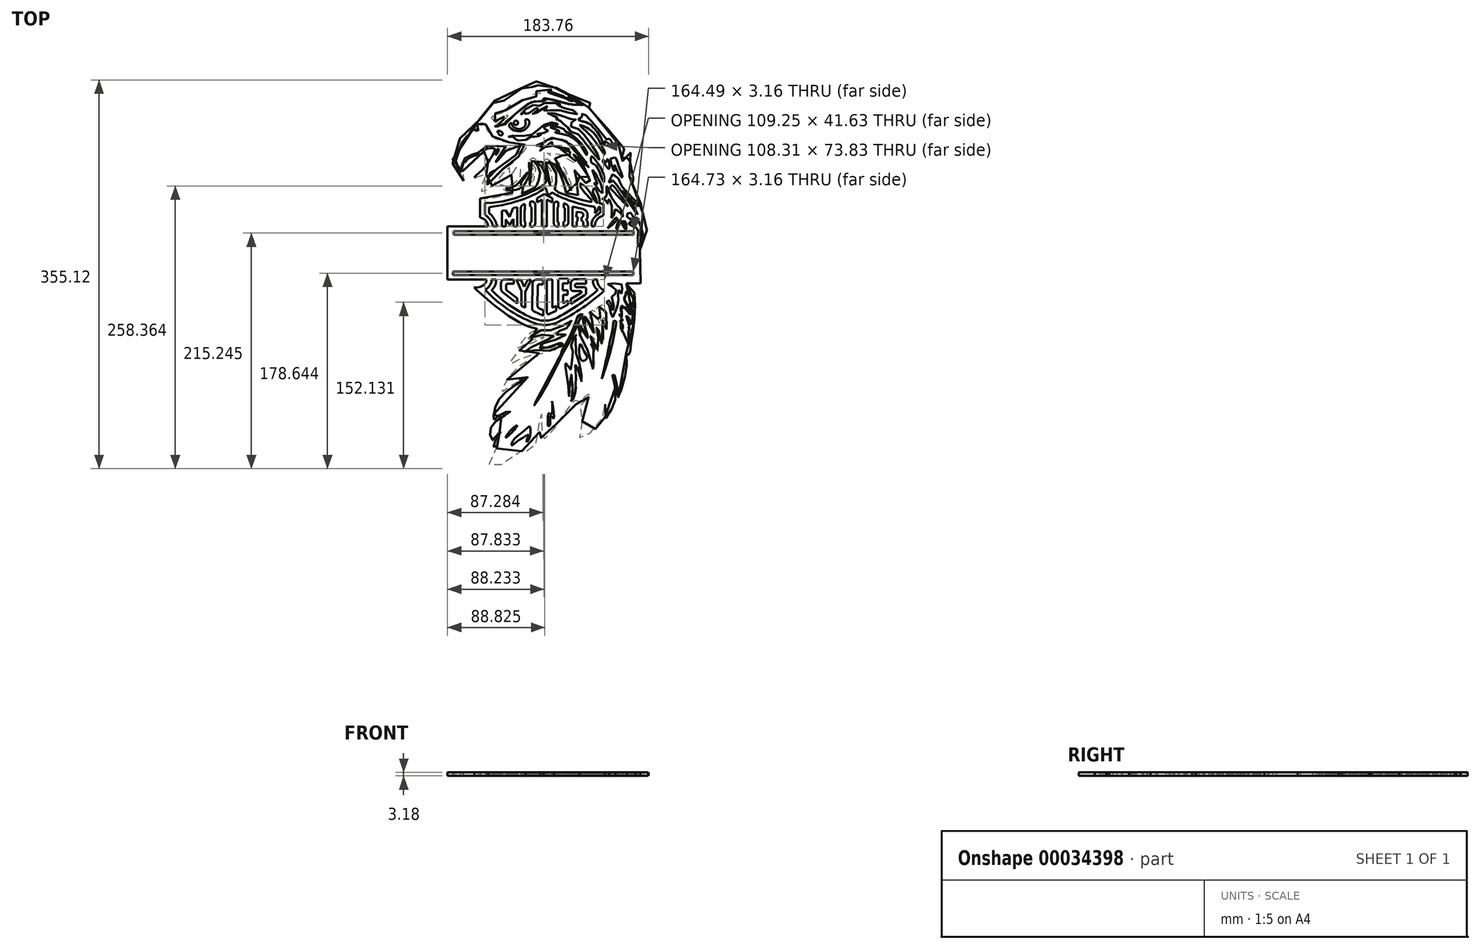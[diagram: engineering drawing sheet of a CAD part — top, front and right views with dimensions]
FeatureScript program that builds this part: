
annotation { "Feature Type Name" : "Feature", "Feature Type Description" : "" }
export const myFeature = defineFeature(function(context is Context, id is Id, definition is map)
    precondition{}
    {
        {
            var Q0;
            Q0=qCreatedBy(makeId("Top.planeOp"),FACE);
            var sketch = newSketch(context, id + "F0", { "sketchPlane" : qUnion([Q0])});
            skFitSpline(sketch, "E0", {"points": [v(60.89, -122.96) * mm, v(51.54, -129.24) * mm, v(44.36, -139.49) * mm, v(55.14, -133.02) * mm, v(69.7, -129.07) * mm, v(55.86, -135.35) * mm, v(43.46, -143.98) * mm, v(37, -153.68) * mm, v(50.3, -147.75) * mm, v(67.55, -144.16) * mm, v(55.18, -149.98) * mm, v(34.66, -167.88) * mm, v(29.99, -179.02) * mm, v(39.87, -172.37) * mm, v(53.35, -166.08) * mm, v(35.2, -177.94) * mm, v(23.52, -194.12) * mm, v(22.27, -204.72) * mm, v(27.48, -200.59) * mm, v(37.36, -197.35) * mm, v(26.76, -204.36) * mm, v(18.86, -216.58) * mm, v(21.56, -223.77) * mm, v(22.81, -221.8) * mm, v(29.28, -215.14) * mm, v(23.17, -225.03) * mm, v(22.82, -230.6) * mm, v(24.97, -227.72) * mm, v(24.61, -232.75) * mm, v(17.71, -249.36) * mm, v(47.08, -234.2) * mm, v(50.68, -230.06) * mm, v(51.76, -230.42) * mm, v(51.76, -234.91) * mm, v(61.28, -226.47) * mm, v(64.5, -198.97) * mm, v(64.69, -197.35) * mm, v(67.75, -211.73) * mm, v(65.06, -224.85) * mm, v(72.96, -218.56) * mm, v(77.45, -213.7) * mm, v(76.91, -210.3) * mm, v(79.97, -208.67) * mm, v(89.85, -194.66) * mm, v(95.42, -189.63) * mm, v(96.86, -187.1) * mm, v(97.76, -191.6) * mm, v(101.71, -185.85) * mm, v(106.38, -183.16) * mm, v(112.5, -178.48) * mm, v(106.56, -186.75) * mm, v(101.9, -190.34) * mm, v(101.72, -204.36) * mm, v(103.51, -202.2) * mm, v(102.98, -208.31) * mm, v(101.6, -214.92) * mm, v(100.96, -222.3) * mm, v(108.91, -218.2) * mm, v(121.85, -203.46) * mm, v(123.64, -190.7) * mm, v(124.9, -192.68) * mm, v(124.19, -203.64) * mm, v(127.78, -199.87) * mm, v(127.78, -197) * mm, v(131.37, -193.4) * mm, v(132.8, -172.43) * mm, v(130.89, -162.53) * mm, v(133.93, -167.3) * mm, v(136.03, -184.24) * mm, v(140.8, -170.9) * mm, v(143.85, -151.3) * mm, v(143.64, -143.5) * mm, v(146.11, -146.35) * mm, v(147.06, -139.68) * mm, v(149.13, -126.23) * mm, v(151.3, -104.9) * mm, v(148.92, -85.61) * mm, v(143.43, -81.43) * mm, v(143.6, -80.34) * mm, v(143.6, -80.34) * mm, v(143.62, -80.34) * mm], "startDerivative": vector(-638.9, -304.7) * mm, "endDerivative": vector(50.3, 16.47) * mm});
            skLineSegment(sketch, "E1", {"start": v(-19.9, -76.89) * mm, "end": v(-19.9, -28.18) * mm});
            skLineSegment(sketch, "E2", {"start": v(-19.9, -28.18) * mm, "end": v(17.02, -28.18) * mm});
            skLineSegment(sketch, "E3", {"start": v(-19.9, -76.89) * mm, "end": v(15.54, -76.89) * mm});
            skFitSpline(sketch, "E4", {"points": [v(15.54, -76.89) * mm, v(15.32, -79.03) * mm, v(9.22, -83.86) * mm, v(4.7, -83.96) * mm, v(4.88, -84.44) * mm, v(28, -104.33) * mm, v(54.6, -119.95) * mm, v(60.89, -121.6) * mm, v(61.95, -122.15) * mm, v(60.89, -122.96) * mm], "startDerivative": vector(-3.74, -30.87) * mm, "endDerivative": vector(-31.67, -17.23) * mm});
            skLineSegment(sketch, "E5", {"start": v(9.74, -20.36) * mm, "end": v(9.74, -2.75) * mm});
            skArc(sketch, "E6", {"start": v(17.02, -28.18) * mm, "mid": v(14.94, -22.81) * mm, "end": v(9.74, -20.36) * mm});
            skFitSpline(sketch, "E7", {"points": [v(9.74, -2.75) * mm, v(22.95, -1.93) * mm, v(37, 0.8) * mm, v(40.65, 1.3) * mm, v(41.3, 2.15) * mm, v(40, 2.65) * mm, v(36.85, 2.73) * mm, v(31.33, 4.59) * mm, v(27.9, 9.1) * mm, v(28.32, 10.25) * mm, v(29.4, 9.46) * mm, v(36.56, 8.46) * mm, v(44.44, 14.19) * mm, v(46.95, 18.63) * mm, v(46.74, 25.15) * mm, v(43.94, 26.51) * mm, v(38.71, 19.5) * mm, v(37.78, 18.06) * mm, v(36.85, 20.35) * mm, v(37.35, 25) * mm, v(37.08, 25.44) * mm, v(36.09, 25.23) * mm, v(23.8, 11.98) * mm, v(18.15, 6.37) * mm, v(13.02, 3.41) * mm, v(11.16, 3.78) * mm, v(13.2, 13.48) * mm, v(15.37, 18.06) * mm, v(15.61, 18.96) * mm, v(14.9, 19.44) * mm, v(12.72, 18.3) * mm, v(4.85, 16.65) * mm, v(5.59, 17.87) * mm, v(11.17, 22.47) * mm, v(17.3, 30.61) * mm, v(21.96, 37.92) * mm, v(23.4, 42) * mm, v(22.96, 42.86) * mm, v(19.7, 43.04) * mm, v(16.87, 42.97) * mm, v(14.26, 41.47) * mm, v(12.28, 39.21) * mm, v(12.03, 38.31) * mm, v(2.12, 35.45) * mm, v(-2.9, 31.62) * mm, v(-5.2, 27.99) * mm, v(-6.06, 20.57) * mm, v(-5.15, 13.5) * mm, v(-5.96, 14.21) * mm, v(-10.17, 17.37) * mm, v(-14.43, 24.11) * mm, v(-15.22, 33.3) * mm, v(-14.53, 39.07) * mm, v(-9.6, 50.6) * mm, v(4.08, 65.75) * mm, v(8.92, 67.99) * mm, v(9.85, 69.57) * mm, v(10.97, 72.18) * mm, v(19.72, 80.07) * mm, v(21.78, 83.42) * mm, v(22.35, 86.77) * mm, v(22.83, 86.2) * mm, v(23.7, 83.33) * mm, v(24.46, 82.37) * mm, v(34.3, 88.63) * mm, v(44.11, 94.7) * mm, v(46.89, 97.58) * mm, v(47.5, 98.3) * mm, v(47.8, 96.29) * mm, v(47.13, 94.33) * mm, v(47.75, 93.75) * mm, v(51.72, 95.33) * mm, v(58.27, 99.73) * mm, v(61.14, 103.41) * mm, v(61.52, 105.47) * mm, v(62.38, 104.7) * mm, v(63.29, 101.74) * mm, v(62.57, 100.26) * mm, v(62.81, 97.72) * mm, v(65.01, 98.3) * mm, v(77.06, 98.73) * mm, v(84.95, 96.1) * mm, v(88.44, 94.23) * mm, v(91.4, 94.7) * mm, v(90.6, 92.7) * mm, v(92.36, 92.22) * mm, v(96.24, 89.35) * mm, v(104.8, 85) * mm, v(115.85, 83.7) * mm, v(115.6, 82.6) * mm, v(112.64, 81.6) * mm, v(109.44, 80.94) * mm, v(109.25, 80.07) * mm, v(110.3, 79.36) * mm, v(117.84, 72.26) * mm, v(130.16, 55.57) * mm, v(133.67, 49.83) * mm, v(140.34, 43.46) * mm, v(141.48, 42.38) * mm, v(140.7, 41.8) * mm, v(137.97, 42.53) * mm, v(136.9, 42.38) * mm, v(136.4, 40.66) * mm, v(139.33, 33.5) * mm, v(140.2, 30.35) * mm, v(141.63, 28.2) * mm, v(143.2, 28.34) * mm, v(144.06, 31.92) * mm, v(145, 42.24) * mm, v(146.07, 43.03) * mm, v(147.07, 40.23) * mm, v(145.78, 25.47) * mm, v(145.93, 19.96) * mm, v(149.94, 16.8) * mm, v(150.23, 15.8) * mm, v(148.36, 15.58) * mm, v(146.21, 17.45) * mm, v(145.14, 16.73) * mm, v(145.5, 15.08) * mm, v(148.65, 11.43) * mm, v(148.65, 9.42) * mm, v(149.22, 1.61) * mm, v(154.81, -6.05) * mm, v(160.69, -9.42) * mm, v(163.7, -9.5) * mm, v(163.4, -10.93) * mm, v(159.33, -12.22) * mm, v(156.75, -11.93) * mm, v(156.96, -13.3) * mm, v(158.68, -16.87) * mm, v(162.26, -31.2) * mm, v(162.84, -41.23) * mm, v(158.4, -48.4) * mm, v(155.81, -49.83) * mm, v(155.74, -50.76) * mm, v(155.71, -50.76) * mm], "startDerivative": vector(961.53, 39.73) * mm, "endDerivative": vector(-56.83, 28.94) * mm});
            skLineSegment(sketch, "E8", {"start": v(143.62, -80.34) * mm, "end": v(156.5, -80.34) * mm});
            skLineSegment(sketch, "E9", {"start": v(156.5, -80.34) * mm, "end": v(155.81, -49.83) * mm});
            skFitSpline(sketch, "E10", {"points": [v(23.99, 30.59) * mm, v(28.8, 38.6) * mm, v(33.39, 45.23) * mm, v(33, 45.3) * mm, v(19.4, 45.49) * mm, v(13.44, 44.04) * mm, v(9.2, 39.96) * mm, v(8.06, 39.1) * mm, v(3.72, 38.46) * mm, v(-1.96, 36.03) * mm, v(-7.08, 29.77) * mm, v(-8.73, 24.14) * mm, v(-8.73, 19.48) * mm, v(-11.34, 24.25) * mm, v(-11.91, 35.29) * mm, v(-8.5, 45.47) * mm, v(-3.04, 54.05) * mm, v(2.25, 59.8) * mm, v(4.92, 59.51) * mm, v(5.89, 58.89) * mm, v(6.63, 57.64) * mm, v(8, 57.98) * mm, v(7.94, 59.74) * mm, v(5.82, 61.24) * mm, v(4.9, 62.15) * mm, v(4.9, 63.6) * mm, v(8.66, 65.72) * mm, v(12.3, 66.48) * mm, v(14.58, 66.36) * mm, v(14.77, 65.3) * mm, v(15.68, 60.74) * mm, v(19.25, 55.58) * mm, v(23.96, 52.1) * mm, v(31.9, 49.47) * mm, v(43.35, 47.65) * mm, v(48.88, 47.22) * mm, v(51.5, 45.61) * mm, v(51.35, 43.04) * mm, v(44.69, 35.25) * mm, v(36.53, 28.17) * mm, v(29.5, 23.34) * mm, v(17, 10.78) * mm, v(15.54, 9.22) * mm, v(14.84, 10.03) * mm, v(15.76, 12.98) * mm, v(17.9, 17) * mm, v(18.87, 20.33) * mm, v(21.5, 22.05) * mm, v(32.88, 29.73) * mm, v(44.42, 38.58) * mm, v(48.88, 43.57) * mm, v(48.23, 45.24) * mm, v(44.74, 45.5) * mm, v(38.3, 43.9) * mm, v(32.56, 39.6) * mm, v(26.17, 32.3) * mm, v(23.99, 30.59) * mm]});
            skFitSpline(sketch, "E11", {"points": [v(51, 68.3) * mm, v(51.95, 69.82) * mm, v(54.15, 68.77) * mm, v(54.91, 66.57) * mm, v(52.23, 61.31) * mm, v(45.92, 58.54) * mm, v(38.75, 60.74) * mm, v(36.36, 64.56) * mm, v(38.17, 66.29) * mm, v(38.75, 64.85) * mm, v(42.57, 61.22) * mm, v(48.5, 61.31) * mm, v(51.56, 65.14) * mm, v(51, 68.3) * mm]});
            skFitSpline(sketch, "E12", {"points": [v(23.2, 67.63) * mm, v(20.27, 70.82) * mm, v(21.93, 73) * mm, v(23.97, 75.29) * mm, v(25.25, 74.4) * mm, v(29.2, 75.16) * mm, v(35.93, 80.9) * mm, v(37.73, 83.16) * mm, v(38.28, 81.54) * mm, v(39.9, 81.9) * mm, v(44.05, 84.7) * mm, v(48.84, 87.23) * mm, v(53.9, 87.77) * mm, v(61.03, 90.38) * mm, v(64.73, 92.64) * mm, v(65.09, 93.63) * mm, v(61.57, 92.82) * mm, v(59.04, 92.1) * mm, v(57.87, 92.73) * mm, v(58.68, 93.82) * mm, v(64.73, 96.16) * mm, v(73.4, 97.16) * mm, v(75.02, 96.52) * mm, v(73.75, 95.8) * mm, v(71.4, 95.44) * mm, v(72.13, 93.72) * mm, v(75.2, 94.27) * mm, v(88.56, 88.85) * mm, v(93.16, 85.78) * mm, v(94.34, 85.7) * mm, v(93.62, 87.13) * mm, v(89.55, 90.11) * mm, v(91.45, 89.75) * mm, v(97.59, 85.87) * mm, v(105, 82.98) * mm, v(103.82, 82.44) * mm, v(100.02, 83.07) * mm, v(94.6, 82.8) * mm, v(84.59, 85.33) * mm, v(70.32, 88.67) * mm, v(66.44, 88.49) * mm, v(66.62, 87.5) * mm, v(68.6, 86.86) * mm, v(68.07, 86.05) * mm, v(60.66, 86.05) * mm, v(53, 83.34) * mm, v(43.78, 75.94) * mm, v(34.21, 68.09) * mm, v(33.13, 67) * mm, v(34.03, 66.28) * mm, v(32.4, 64.53) * mm, v(29.03, 64.26) * mm, v(23.51, 62.7) * mm, v(23.18, 63.48) * mm, v(29.72, 68.24) * mm, v(35.23, 72.76) * mm, v(35.23, 73.45) * mm, v(32.04, 72.16) * mm, v(26.68, 68.6) * mm, v(24.9, 67.1) * mm, v(23.2, 67.63) * mm]});
            skFitSpline(sketch, "E13", {"points": [v(28.62, 54.78) * mm, v(26.77, 56.39) * mm, v(25.8, 58.64) * mm, v(28.3, 58.72) * mm, v(30.55, 56.47) * mm, v(28.62, 54.78) * mm]});
            skFitSpline(sketch, "E14", {"points": [v(132.62, 42.72) * mm, v(130.18, 48.4) * mm, v(127.48, 52.33) * mm, v(126.4, 50.84) * mm, v(124.77, 52.06) * mm, v(113, 66.12) * mm, v(103.67, 74.65) * mm, v(102.59, 73.3) * mm, v(102.72, 71.8) * mm, v(101.37, 70.86) * mm, v(99.88, 69.1) * mm, v(108.4, 66.26) * mm, v(113.81, 61.53) * mm, v(119.63, 53.95) * mm, v(123.55, 45.3) * mm, v(123.69, 49.49) * mm, v(125.58, 48.54) * mm, v(129.91, 45.3) * mm, v(132.62, 42.72) * mm]});
            skFitSpline(sketch, "E15", {"points": [v(38.77, -226.87) * mm, v(41.77, -221.5) * mm, v(49.5, -215.5) * mm, v(55.3, -210.99) * mm, v(55.73, -218.72) * mm, v(53.88, -223.7) * mm, v(52.4, -224.85) * mm, v(52.93, -222.23) * mm, v(54, -218.66) * mm, v(50.96, -220.1) * mm, v(43.37, -224.85) * mm, v(38.81, -228.18) * mm, v(38.77, -226.87) * mm]});
            skFitSpline(sketch, "E16", {"points": [v(26.96, 41.34) * mm, v(25.44, 38.45) * mm, v(24.3, 37.24) * mm, v(23.92, 38.83) * mm, v(24.83, 40.35) * mm, v(25.44, 42.17) * mm, v(26.73, 42.48) * mm, v(26.96, 41.34) * mm]});
            skFitSpline(sketch, "E17", {"points": [v(47.03, 74.12) * mm, v(49.91, 77.76) * mm, v(56.14, 81.7) * mm, v(61, 82.92) * mm, v(64.49, 81.86) * mm, v(67.37, 83.68) * mm, v(73.14, 84.74) * mm, v(83.31, 83.07) * mm, v(81.5, 81.56) * mm, v(86.8, 79.58) * mm, v(94.25, 77.91) * mm, v(99.1, 74.88) * mm, v(95.61, 74.42) * mm, v(88.32, 76.4) * mm, v(80.13, 78.06) * mm, v(71.62, 77.6) * mm, v(68.59, 77.46) * mm, v(69.8, 79.89) * mm, v(71.02, 81.56) * mm, v(68.44, 81.4) * mm, v(65.7, 77.6) * mm, v(61, 75.48) * mm, v(58.7, 73.74) * mm, v(58.03, 74.46) * mm, v(59.18, 75.83) * mm, v(63.74, 79.53) * mm, v(62.8, 80.43) * mm, v(59.78, 78.98) * mm, v(53.21, 74.3) * mm, v(51.95, 73.7) * mm, v(51.6, 74.9) * mm, v(51.95, 76.6) * mm, v(49.85, 75.7) * mm, v(47.76, 73.19) * mm, v(47.03, 74.12) * mm]});
            skFitSpline(sketch, "E18", {"points": [v(123.88, 38.5) * mm, v(119.96, 47.12) * mm, v(112.2, 58.45) * mm, v(101.04, 64.5) * mm, v(101.64, 63.4) * mm, v(107.52, 57.94) * mm, v(113.9, 50.7) * mm, v(121.32, 40.13) * mm, v(123.5, 37.33) * mm, v(123.4, 38.08) * mm, v(123.88, 38.5) * mm]});
            skFitSpline(sketch, "E19", {"points": [v(132.74, 35.06) * mm, v(131.26, 34.04) * mm, v(129.44, 33.92) * mm, v(130.66, 25.9) * mm, v(132.58, 22.12) * mm, v(132.23, 27.62) * mm, v(133.08, 26.87) * mm, v(135.81, 21.07) * mm, v(139.85, 16.5) * mm, v(137.18, 25.13) * mm, v(132.74, 35.06) * mm]});
            skFitSpline(sketch, "E20", {"points": [v(98.35, -112.13) * mm, v(88.79, -134.57) * mm, v(84.73, -141.6) * mm, v(84.4, -143.42) * mm, v(59.12, -191.64) * mm, v(62.99, -186.77) * mm, v(81.68, -151.84) * mm, v(85.87, -143.35) * mm, v(94.53, -127.62) * mm, v(100.48, -113.94) * mm, v(101.2, -112.27) * mm, v(101.52, -111.84) * mm, v(103.04, -109.46) * mm, v(102.92, -108.2) * mm, v(98.93, -110.41) * mm, v(98.35, -112.13) * mm]});
            skFitSpline(sketch, "E21", {"points": [v(144.83, -85.14) * mm, v(148.17, -90.56) * mm, v(150.42, -97.6) * mm, v(149.97, -102.47) * mm, v(148.17, -98.23) * mm, v(146.81, -98.32) * mm, v(147.36, -102.02) * mm, v(149.16, -105.18) * mm, v(149.16, -110.15) * mm, v(148.26, -117.73) * mm, v(145.28, -111.32) * mm, v(143.38, -110.42) * mm, v(143.83, -113.58) * mm, v(146.45, -119.72) * mm, v(147.9, -123.33) * mm, v(146.54, -122.79) * mm, v(144.74, -120.26) * mm, v(144.83, -123.87) * mm, v(146.1, -126.58) * mm, v(145.73, -136.6) * mm, v(143.65, -130.37) * mm, v(138.69, -123.5) * mm, v(138.15, -120.35) * mm, v(139.86, -121.88) * mm, v(139.86, -118) * mm, v(137.7, -114.4) * mm, v(139.77, -114.4) * mm, v(137.79, -110.15) * mm, v(137.06, -108.61) * mm, v(139.23, -109.52) * mm, v(138.5, -105.63) * mm, v(138.78, -101.4) * mm, v(139.6, -100.4) * mm, v(139.6, -102.02) * mm, v(141.22, -102.93) * mm, v(142.12, -101.75) * mm, v(144.65, -105.27) * mm, v(145.37, -106.72) * mm, v(146.9, -108.61) * mm, v(147.9, -106.9) * mm, v(143.65, -99.31) * mm, v(141.3, -94.35) * mm, v(142.3, -91.28) * mm, v(143.3, -90.1) * mm, v(142.84, -88.48) * mm, v(143.56, -87.49) * mm, v(145.1, -89.84) * mm, v(146.27, -89.2) * mm, v(144.3, -86.84) * mm, v(144.83, -85.14) * mm]});
            skFitSpline(sketch, "E22", {"points": [v(75.56, -187.9) * mm, v(77, -196.64) * mm, v(76.85, -203.8) * mm, v(75.79, -203.28) * mm, v(74.82, -201.4) * mm, v(73.85, -201.69) * mm, v(73.97, -204.08) * mm, v(73.51, -210.27) * mm, v(72.38, -210.84) * mm, v(71.75, -209.7) * mm, v(71.86, -201.29) * mm, v(72.26, -199.01) * mm, v(73.97, -199.53) * mm, v(75.45, -199.3) * mm, v(75.56, -187.9) * mm]});
            skFitSpline(sketch, "E23", {"points": [v(43.78, -210.05) * mm, v(37.19, -215.17) * mm, v(33.2, -221.2) * mm, v(38.44, -216.88) * mm, v(43.78, -210.05) * mm]});
            skFitSpline(sketch, "E24", {"points": [v(90.95, -183.78) * mm, v(89.88, -167.23) * mm, v(87.15, -152.35) * mm, v(90.95, -157.36) * mm, v(92.77, -158.88) * mm, v(93.98, -149.01) * mm, v(94.6, -142.79) * mm, v(92.92, -139.3) * mm, v(94.29, -132.46) * mm, v(97.17, -127.3) * mm, v(97.02, -131.1) * mm, v(98.4, -148.46) * mm, v(101.38, -155.78) * mm, v(102.67, -170.01) * mm, v(100.34, -161.49) * mm, v(96.88, -153.52) * mm, v(97.04, -159.31) * mm, v(97.12, -177.73) * mm, v(94.39, -186.58) * mm, v(93.18, -187.62) * mm, v(93.9, -182.96) * mm, v(94.22, -180.7) * mm, v(93.34, -163.82) * mm, v(92.13, -167.36) * mm, v(90.95, -183.78) * mm]});
            skFitSpline(sketch, "E25", {"points": [v(65.37, -123.04) * mm, v(58.77, -126.8) * mm, v(53.2, -131.12) * mm, v(59.8, -128.5) * mm, v(67.42, -127.14) * mm, v(76.86, -128.05) * mm, v(76.97, -129.53) * mm, v(75.15, -130.32) * mm, v(58.26, -137.57) * mm, v(49.82, -142.96) * mm, v(53.92, -142) * mm, v(65.26, -141.43) * mm, v(77.97, -141.03) * mm, v(85.37, -135.88) * mm, v(82.07, -135) * mm, v(76.12, -137.97) * mm, v(67.6, -139.42) * mm, v(64.46, -139.34) * mm, v(66.23, -137.33) * mm, v(65.26, -136.6) * mm, v(67.27, -135) * mm, v(79.82, -131.62) * mm, v(87.94, -127.6) * mm, v(87.06, -126.47) * mm, v(79.18, -126.8) * mm, v(77.4, -125.83) * mm, v(83.84, -123.41) * mm, v(85.29, -123.17) * mm, v(91.96, -118.75) * mm, v(93.65, -114.73) * mm, v(89.55, -116.74) * mm, v(80.7, -120.84) * mm, v(70.9, -123.57) * mm, v(65.37, -123.04) * mm]});
            skFitSpline(sketch, "E26", {"points": [v(138.95, -89.7) * mm, v(139.66, -83.4) * mm, v(138.52, -81.1) * mm, v(126.8, -80.75) * mm, v(130.74, -83.33) * mm, v(134.6, -87.57) * mm, v(131.92, -90.85) * mm, v(129.78, -93.43) * mm, v(131.78, -98.02) * mm, v(131.35, -104.75) * mm, v(129.49, -99.02) * mm, v(126.77, -95.87) * mm, v(125.48, -97.3) * mm, v(128.06, -101.17) * mm, v(130.5, -111.35) * mm, v(134.07, -104.04) * mm, v(136.22, -97.45) * mm, v(135.8, -90) * mm, v(136.8, -86.55) * mm, v(138.95, -89.7) * mm]});
            skFitSpline(sketch, "E27", {"points": [v(125.47, -122.46) * mm, v(126.33, -113.57) * mm, v(124.04, -103.83) * mm, v(122.17, -100.1) * mm, v(118.4, -101.84) * mm, v(116.15, -103.26) * mm, v(118.16, -106.7) * mm, v(120.31, -118.02) * mm, v(118.45, -115.3) * mm, v(115.15, -107.27) * mm, v(113.58, -104.98) * mm, v(108.13, -108.7) * mm, v(109.28, -111) * mm, v(113.15, -117.44) * mm, v(114.58, -126.76) * mm, v(111.14, -119.16) * mm, v(106.27, -111.43) * mm, v(104.83, -110.7) * mm, v(103.69, -113.43) * mm, v(106.84, -123.75) * mm, v(108.13, -130.34) * mm, v(104.7, -125.33) * mm, v(102.11, -121.89) * mm, v(101.54, -118.6) * mm, v(100.1, -119.6) * mm, v(100.53, -123.75) * mm, v(101.4, -128.62) * mm, v(105.98, -136.07) * mm, v(109.56, -146.96) * mm, v(113, -158.43) * mm, v(114.44, -153.41) * mm, v(112.29, -139.8) * mm, v(111, -135.93) * mm, v(114.72, -141.38) * mm, v(110.57, -129.91) * mm, v(111.14, -128.34) * mm, v(116.01, -135.36) * mm, v(117.59, -142.8) * mm, v(118.16, -134.78) * mm, v(116.01, -123.75) * mm, v(116.15, -120.88) * mm, v(119.6, -127.33) * mm, v(120.31, -135.07) * mm, v(121.89, -134.07) * mm, v(122.17, -112.43) * mm, v(123.46, -112) * mm, v(125.47, -122.46) * mm]});
            skFitSpline(sketch, "E28", {"points": [v(101.2, -135.5) * mm, v(101.1, -148.12) * mm, v(104.17, -151.07) * mm, v(107.46, -148.57) * mm, v(104.28, -141.18) * mm, v(101.2, -135.5) * mm]});
            skFitSpline(sketch, "E29", {"points": [v(155.08, -47.17) * mm, v(157.79, -44.1) * mm, v(157.97, -32) * mm, v(152.91, -20.08) * mm, v(153.63, -24.96) * mm, v(152.19, -24.42) * mm, v(149.3, -18.28) * mm, v(146.41, -15.57) * mm, v(143.7, -18.28) * mm, v(148.22, -22.97) * mm, v(148.22, -24.96) * mm, v(145.5, -24.96) * mm, v(147.5, -27.49) * mm, v(153.27, -30.01) * mm, v(154, -36.88) * mm, v(155.08, -47.17) * mm]});
            skFitSpline(sketch, "E30", {"points": [v(129.93, -20.4) * mm, v(130.5, -11.05) * mm, v(126.8, -3.14) * mm, v(126.63, -7.51) * mm, v(124.39, -4.21) * mm, v(121.43, -3.08) * mm, v(125, -1.12) * mm, v(125.57, 1.84) * mm, v(125.68, 8.32) * mm, v(128.07, 2.07) * mm, v(133.19, -6.7) * mm, v(136.14, -9.99) * mm, v(139.44, -14.2) * mm, v(140.24, -19.32) * mm, v(136.83, -14.54) * mm, v(133, -13.04) * mm, v(132.4, -16.68) * mm, v(129.93, -20.4) * mm]});
            skFitSpline(sketch, "E31", {"points": [v(53.52, 21.4) * mm, v(49.3, 16.7) * mm, v(42.67, 9.47) * mm, v(35.44, 6.58) * mm, v(33.27, 6.58) * mm, v(35.8, 4.9) * mm, v(47.25, 7.18) * mm, v(47.13, 10.67) * mm, v(50.77, 16.85) * mm, v(53.52, 21.4) * mm]});
            skFitSpline(sketch, "E32", {"points": [v(54.71, 30.37) * mm, v(54.86, 27.34) * mm, v(55.27, 18.83) * mm, v(51.22, 12.05) * mm, v(48.1, 1.89) * mm, v(56.55, 5.8) * mm, v(61.4, 8.51) * mm, v(61.92, 10.21) * mm, v(64.2, 16.2) * mm, v(63.53, 25.22) * mm, v(59.44, 30.52) * mm, v(59.62, 31.66) * mm, v(62.57, 29.8) * mm, v(68.9, 21.78) * mm, v(69.98, 11.48) * mm, v(67.96, 9.62) * mm, v(55.04, 2.46) * mm, v(28.13, -5.86) * mm, v(14.18, -7.08) * mm], "startDerivative": vector(-4.46, -71.4) * mm, "endDerivative": vector(-161.05, -10.37) * mm});
            skLineSegment(sketch, "E33", {"start": v(14.18, -7.08) * mm, "end": v(14.18, -17.6) * mm});
            skLineSegment(sketch, "E34", {"start": v(17.93, -10.61) * mm, "end": v(17.93, -15.98) * mm});
            skLineSegment(sketch, "E35", {"start": v(122.49, -7.66) * mm, "end": v(122.49, -18.19) * mm});
            skLineSegment(sketch, "E36", {"start": v(119.72, -10.67) * mm, "end": v(119.72, -15.91) * mm});
            skLineSegment(sketch, "E37.bottom", {"start": v(-14.3, -32.8) * mm, "end": v(150.18, -32.8) * mm});
            skLineSegment(sketch, "E37.top", {"start": v(-14.3, -35.97) * mm, "end": v(150.18, -35.97) * mm});
            skLineSegment(sketch, "E37.left", {"start": v(-14.3, -32.8) * mm, "end": v(-14.3, -35.97) * mm});
            skLineSegment(sketch, "E37.right", {"start": v(150.18, -32.8) * mm, "end": v(150.18, -35.97) * mm});
            skLineSegment(sketch, "E38.bottom", {"start": v(149.75, -69.4) * mm, "end": v(-14.98, -69.4) * mm});
            skLineSegment(sketch, "E38.top", {"start": v(149.75, -72.57) * mm, "end": v(-14.98, -72.57) * mm});
            skLineSegment(sketch, "E38.left", {"start": v(149.75, -69.4) * mm, "end": v(149.75, -72.57) * mm});
            skLineSegment(sketch, "E38.right", {"start": v(-14.98, -69.4) * mm, "end": v(-14.98, -72.57) * mm});
            skArc(sketch, "E39", {"start": v(21.61, -28.18) * mm, "mid": v(18.97, -22.14) * mm, "end": v(14.18, -17.6) * mm});
            skFitSpline(sketch, "E40", {"points": [v(71.55, 75.37) * mm, v(76.71, 75.18) * mm, v(86.45, 71.93) * mm, v(94.29, 69.64) * mm, v(97.06, 69.64) * mm, v(96.39, 68.02) * mm, v(92.57, 66.2) * mm, v(92.38, 63.53) * mm, v(98.59, 61.23) * mm, v(104.13, 56.17) * mm, v(113.68, 43.18) * mm, v(119.03, 32.87) * mm, v(117.79, 33.25) * mm, v(112.34, 40.22) * mm, v(103.74, 50.63) * mm, v(101.16, 54.64) * mm, v(93.43, 58.08) * mm, v(90.66, 59.9) * mm, v(89.9, 62.57) * mm, v(87.03, 64.77) * mm, v(83.97, 66.58) * mm, v(83.78, 67.85) * mm, v(83.22, 68.87) * mm, v(81.2, 68.95) * mm, v(79.8, 69.18) * mm, v(79.9, 71.28) * mm, v(77.25, 73.07) * mm, v(71.54, 74.8) * mm, v(71.55, 75.37) * mm]});
            skFitSpline(sketch, "E41", {"points": [v(125.96, 33.13) * mm, v(127.85, 28.7) * mm, v(127.5, 24.3) * mm, v(124.25, 27.9) * mm, v(121.9, 31.5) * mm, v(122.35, 32.58) * mm, v(124.43, 29.88) * mm, v(125.96, 33.13) * mm]});
            skFitSpline(sketch, "E42", {"points": [v(111.63, 35.67) * mm, v(111.65, 30.02) * mm, v(115.62, 27.4) * mm, v(122.83, 12.17) * mm, v(122.74, 18.66) * mm, v(117.42, 29.3) * mm, v(111.63, 35.67) * mm]});
            skFitSpline(sketch, "E43", {"points": [v(112.64, 23.52) * mm, v(117.65, 15.48) * mm, v(120.98, 7.9) * mm, v(121.13, 2.29) * mm, v(114.42, 11.37) * mm, v(116.59, 10.32) * mm, v(116.23, 13.19) * mm, v(114.77, 16.39) * mm, v(112.64, 23.52) * mm]});
            skFitSpline(sketch, "E44", {"points": [v(113.88, 7.15) * mm, v(112.52, 4.25) * mm, v(113.88, 0.96) * mm, v(116.93, -5.7) * mm, v(116.53, -7.23) * mm, v(114.04, -3.78) * mm, v(109.54, 3.85) * mm, v(102.64, 10.84) * mm, v(100.87, 10.84) * mm, v(101.83, 7.23) * mm, v(107.54, 0) * mm, v(112.68, -5.79) * mm, v(110.99, -5.79) * mm, v(95.4, -2.17) * mm, v(77.9, 4.97) * mm, v(78.14, 6.18) * mm, v(79.74, 15.9) * mm, v(77.25, 24.85) * mm, v(72.4, 30.81) * mm, v(76.06, 29.53) * mm, v(83.63, 18.73) * mm, v(88.57, 2.4) * mm], "startDerivative": vector(-59.85, -89.52) * mm, "endDerivative": vector(54.44, -221.95) * mm});
            skFitSpline(sketch, "E45", {"points": [v(54.71, 30.37) * mm, v(58.14, 26.37) * mm, v(58.43, 17.45) * mm, v(54.86, 9.65) * mm, v(57.07, 11.48) * mm, v(60.22, 17.45) * mm, v(60.58, 25.4) * mm, v(56.28, 32.48) * mm, v(54.71, 33.4) * mm, v(54.71, 34.48) * mm, v(57.07, 34.7) * mm, v(63.3, 32.62) * mm, v(67.8, 29.47) * mm, v(71.6, 23.25) * mm, v(73.81, 15.45) * mm, v(73.81, 8.8) * mm, v(75.6, 11.48) * mm, v(76.4, 18.16) * mm, v(72.88, 26.1) * mm, v(67.73, 33.33) * mm, v(67.45, 34.48) * mm, v(68.9, 34.26) * mm, v(75.32, 31.97) * mm, v(82.62, 26.04) * mm, v(89.49, 15.3) * mm, v(92.28, 3.71) * mm, v(93.28, 6.93) * mm, v(89.99, 19.52) * mm, v(80.11, 32.48) * mm, v(70.6, 37.77) * mm, v(70.52, 38.56) * mm, v(72.17, 38.99) * mm, v(81.83, 37.91) * mm, v(99.08, 27.97) * mm, v(99.93, 27.34) * mm, v(94.85, 34.05) * mm, v(85.12, 41.56) * mm, v(82.26, 42.85) * mm, v(84.62, 42.85) * mm, v(91.06, 40.13) * mm, v(93.78, 39.49) * mm, v(94.71, 39.34) * mm, v(90.27, 43) * mm, v(79.54, 45.78) * mm, v(75.46, 45.57) * mm, v(75.53, 47) * mm, v(77.4, 48.8) * mm, v(76.4, 49.08) * mm, v(73.46, 47.86) * mm, v(66.37, 42.28) * mm, v(63.58, 40.63) * mm, v(62.65, 41.42) * mm, v(63.44, 42.56) * mm, v(67.16, 44.71) * mm, v(66.3, 44.85) * mm, v(63.22, 44.64) * mm, v(60.86, 44.93) * mm, v(61.92, 46.14) * mm, v(66.09, 47.29) * mm, v(68.9, 48.1) * mm, v(69.2, 49.38) * mm, v(68.12, 50.53) * mm, v(68.44, 51.96) * mm, v(70.23, 51.74) * mm, v(72.1, 50.5) * mm, v(72.63, 51.46) * mm, v(73.67, 52.64) * mm, v(76.24, 52.39) * mm, v(81.54, 49.81) * mm, v(84.3, 49.2) * mm, v(84.61, 50.5) * mm, v(85.54, 51.24) * mm, v(86.87, 50.64) * mm, v(94.11, 45.86) * mm, v(103.35, 35.56) * mm, v(109.07, 25.54) * mm, v(107.42, 26.47) * mm, v(103.99, 31.27) * mm, v(96.26, 37.5) * mm, v(95.12, 37.63) * mm, v(96.05, 35.99) * mm, v(100.2, 32.63) * mm, v(106.28, 24.11) * mm, v(110.14, 13.88) * mm, v(111.15, 8.66) * mm, v(110, 9.01) * mm, v(104.28, 13.23) * mm, v(98.34, 20.1) * mm, v(94.62, 25.26) * mm, v(94.33, 25.54) * mm, v(97.94, 14.94) * mm, v(98.79, 6.2) * mm, v(99.02, -0.96) * mm, v(97.88, -0.8) * mm, v(88.57, 2.4) * mm], "startDerivative": vector(341.57, -304.33) * mm, "endDerivative": vector(-733.81, 236.52) * mm});
            skFitSpline(sketch, "E46", {"points": [v(80.58, 65.6) * mm, v(76.29, 66.67) * mm, v(68.2, 64.47) * mm, v(61.39, 58.68) * mm, v(55.22, 55.09) * mm, v(42.03, 54.55) * mm, v(36.67, 54.23) * mm, v(35.97, 53.59) * mm, v(37.15, 53.05) * mm, v(42.73, 53.16) * mm, v(42.2, 51.4) * mm, v(42.35, 50.26) * mm, v(46.21, 50.32) * mm, v(53.3, 51.23) * mm, v(56.88, 54.07) * mm, v(59.56, 54.07) * mm, v(60.42, 53.43) * mm, v(63.15, 54.34) * mm, v(66.05, 54.71) * mm, v(65.25, 55.62) * mm, v(61.87, 55.9) * mm, v(64.17, 56.75) * mm, v(70.4, 57.55) * mm, v(71.95, 58.95) * mm, v(71.04, 60.93) * mm, v(68.3, 60.5) * mm, v(67.44, 61.58) * mm, v(68.73, 62.86) * mm, v(73.77, 64.52) * mm, v(81.6, 64.52) * mm, v(81.09, 65.1) * mm, v(80.58, 65.6) * mm]});
            skCircle(sketch, "E47", {"center": v(42.63, 66.36) * mm, "radius": 1.93 * mm});
            skFitSpline(sketch, "E48", {"points": [v(74, 62.38) * mm, v(79.9, 62.8) * mm, v(87.18, 59.9) * mm, v(88.25, 57.87) * mm, v(90.72, 57.01) * mm, v(100.58, 49.3) * mm, v(107.45, 38.9) * mm, v(107.45, 36.86) * mm, v(106.27, 38.68) * mm, v(99.73, 48) * mm, v(89.43, 55.09) * mm, v(78.39, 57.55) * mm, v(79.57, 57.98) * mm, v(82.68, 58.3) * mm, v(80.53, 59.8) * mm, v(74, 62.38) * mm]});
            skFitSpline(sketch, "E49", {"points": [v(144.94, -9.87) * mm, v(137.62, 0.85) * mm, v(130.5, 9.44) * mm, v(129.28, 8.5) * mm, v(128.6, 7.23) * mm, v(131.14, 4.19) * mm, v(139.44, -4.55) * mm, v(144.94, -9.87) * mm]});
            skFitSpline(sketch, "E50", {"points": [v(154.5, -8.7) * mm, v(144.37, 2.54) * mm, v(137.7, 11.78) * mm, v(136.9, 14.67) * mm, v(130.8, 19.17) * mm, v(130.07, 17.88) * mm, v(127.42, 12.34) * mm, v(127.58, 11.54) * mm, v(130.24, 13.7) * mm, v(131.6, 13.23) * mm, v(140.76, 1.26) * mm, v(153.6, -17.21) * mm, v(148.63, -7.66) * mm, v(140.12, 4.23) * mm, v(146.7, -3.08) * mm, v(152.16, -8.38) * mm, v(154.57, -9.66) * mm, v(154.5, -8.7) * mm]});
            skFitSpline(sketch, "E51", {"points": [v(113.88, 7.15) * mm, v(115.55, 5.33) * mm, v(118.61, -2.34) * mm, v(118.84, -6.77) * mm, v(118.8, -7.05) * mm, v(122.49, -7.66) * mm], "startDerivative": vector(9.11, -7.78) * mm, "endDerivative": vector(24.23, -2.54) * mm});
            skLineSegment(sketch, "E52", {"start": v(21.61, -28.18) * mm, "end": v(25.43, -28.18) * mm});
            skLineSegment(sketch, "E53", {"start": v(111.72, -28.18) * mm, "end": v(114.6, -28.18) * mm});
            skFitSpline(sketch, "E54", {"points": [v(122.49, -18.19) * mm, v(117.02, -21.6) * mm, v(114.6, -28.18) * mm], "startDerivative": vector(-12.43, -5.64) * mm, "endDerivative": vector(-0.66, -15.6) * mm});
            skFitSpline(sketch, "E55", {"points": [v(111.72, -28.18) * mm, v(113.7, -20.6) * mm, v(119.72, -15.91) * mm], "startDerivative": vector(-2.08, 14.93) * mm, "endDerivative": vector(14.14, 7.93) * mm});
            skFitSpline(sketch, "E56", {"points": [v(25.43, -28.18) * mm, v(22.17, -20.52) * mm, v(17.93, -15.98) * mm], "startDerivative": vector(-5.14, 16.11) * mm, "endDerivative": vector(-10, 8.76) * mm});
            skFitSpline(sketch, "E57", {"points": [v(119.72, -10.67) * mm, v(108, -9.2) * mm, v(77.08, 1.9) * mm, v(69.85, 6.73) * mm, v(62.59, 2.54) * mm, v(33.1, -8.22) * mm, v(17.93, -10.61) * mm], "startDerivative": vector(-76.98, 8.59) * mm, "endDerivative": vector(-92.04, -13) * mm});
            skFitSpline(sketch, "E58", {"points": [v(69.85, 6.73) * mm, v(70.6, 4.35) * mm, v(72.48, 0.82) * mm, v(75.85, 2.73) * mm], "startDerivative": vector(3.6, -7.6) * mm, "endDerivative": vector(13.15, 7.65) * mm});
            skFitSpline(sketch, "E59", {"points": [v(114.05, -10.03) * mm, v(115.1, -13.17) * mm, v(115.2, -16.1) * mm, v(117.5, -12.64) * mm, v(118.03, -10.5) * mm, v(118.04, -10.5) * mm], "startDerivative": vector(5.76, -10.78) * mm, "endDerivative": vector(0.89, -0.44) * mm});
            skFitSpline(sketch, "E60.trimOffspring", {"points": [v(119.72, -10.67) * mm, v(108, -9.2) * mm, v(77.08, 1.9) * mm, v(69.85, 6.73) * mm, v(62.59, 2.54) * mm, v(33.1, -8.22) * mm, v(17.93, -10.61) * mm], "startDerivative": vector(-76.98, 8.59) * mm, "endDerivative": vector(-92.04, -13) * mm});
            skLineSegment(sketch, "E61", {"start": v(29.73, -28.18) * mm, "end": v(29.73, -13.83) * mm});
            skLineSegment(sketch, "E62", {"start": v(40.16, -28.18) * mm, "end": v(43.8, -28.18) * mm});
            skLineSegment(sketch, "E63", {"start": v(43.8, -28.18) * mm, "end": v(43.8, -10.75) * mm});
            skLineSegment(sketch, "E64", {"start": v(43.8, -10.75) * mm, "end": v(40.11, -11.54) * mm});
            skLineSegment(sketch, "E65", {"start": v(40.11, -11.54) * mm, "end": v(36.86, -19.55) * mm});
            skLineSegment(sketch, "E66", {"start": v(36.86, -19.55) * mm, "end": v(33.33, -13.48) * mm});
            skLineSegment(sketch, "E67", {"start": v(33.33, -13.48) * mm, "end": v(29.73, -13.83) * mm});
            skLineSegment(sketch, "E68", {"start": v(29.73, -28.18) * mm, "end": v(33.34, -28.18) * mm});
            skLineSegment(sketch, "E69", {"start": v(33.34, -28.18) * mm, "end": v(33.34, -21.96) * mm});
            skLineSegment(sketch, "E70", {"start": v(33.34, -21.96) * mm, "end": v(36.66, -27.06) * mm});
            skLineSegment(sketch, "E71", {"start": v(36.66, -27.06) * mm, "end": v(40.16, -21.68) * mm});
            skLineSegment(sketch, "E72", {"start": v(40.16, -21.68) * mm, "end": v(40.16, -28.18) * mm});
            skLineSegment(sketch, "E73", {"start": v(68.54, 1.4) * mm, "end": v(61.81, -2.55) * mm});
            skLineSegment(sketch, "E74", {"start": v(61.81, -2.55) * mm, "end": v(61.81, -6.25) * mm});
            skLineSegment(sketch, "E75", {"start": v(61.81, -6.25) * mm, "end": v(66.31, -3.83) * mm});
            skLineSegment(sketch, "E76", {"start": v(66.31, -3.83) * mm, "end": v(66.31, -28.18) * mm});
            skLineSegment(sketch, "E77", {"start": v(66.31, -28.18) * mm, "end": v(70.72, -28.18) * mm});
            skLineSegment(sketch, "E78", {"start": v(70.72, -28.18) * mm, "end": v(70.72, -3.75) * mm});
            skLineSegment(sketch, "E79", {"start": v(70.72, -3.75) * mm, "end": v(75.76, -6.26) * mm});
            skLineSegment(sketch, "E80", {"start": v(75.76, -6.26) * mm, "end": v(75.76, -2.43) * mm});
            skLineSegment(sketch, "E81", {"start": v(75.76, -2.43) * mm, "end": v(68.54, 1.4) * mm});
            skLineSegment(sketch, "E82", {"start": v(94.35, -10.25) * mm, "end": v(94.35, -28.18) * mm});
            skLineSegment(sketch, "E83", {"start": v(94.35, -28.18) * mm, "end": v(97.93, -28.18) * mm});
            skLineSegment(sketch, "E84", {"start": v(97.93, -28.18) * mm, "end": v(97.93, -23.7) * mm});
            skLineSegment(sketch, "E85", {"start": v(97.93, -23.7) * mm, "end": v(98.82, -23.7) * mm});
            skLineSegment(sketch, "E86", {"start": v(98.82, -23.7) * mm, "end": v(98.88, -19.8) * mm});
            skLineSegment(sketch, "E87", {"start": v(98.88, -19.8) * mm, "end": v(97.77, -19.79) * mm});
            skLineSegment(sketch, "E88", {"start": v(97.77, -19.79) * mm, "end": v(98.1, -14.76) * mm});
            skLineSegment(sketch, "E89", {"start": v(98.1, -14.76) * mm, "end": v(102.32, -15.54) * mm});
            skLineSegment(sketch, "E90", {"start": v(104.1, -24.8) * mm, "end": v(104.1, -28.18) * mm});
            skLineSegment(sketch, "E91", {"start": v(104.1, -28.18) * mm, "end": v(108.08, -28.18) * mm});
            skLineSegment(sketch, "E92", {"start": v(108.08, -28.18) * mm, "end": v(108.08, -24.81) * mm});
            skLineSegment(sketch, "E93", {"start": v(77.1, -8.25) * mm, "end": v(77.1, -25.13) * mm});
            skLineSegment(sketch, "E94", {"start": v(90.57, -10.83) * mm, "end": v(90.57, -24.11) * mm});
            skLineSegment(sketch, "E95", {"start": v(47.04, -11.67) * mm, "end": v(47.04, -25.65) * mm});
            skLineSegment(sketch, "E96", {"start": v(60.22, -8.49) * mm, "end": v(60.22, -25.35) * mm});
            skLineSegment(sketch, "E97", {"start": v(56.82, -11.78) * mm, "end": v(56.82, -23.04) * mm});
            skLineSegment(sketch, "E98", {"start": v(55.54, -5.95) * mm, "end": v(55.54, -9.8) * mm});
            skLineSegment(sketch, "E99", {"start": v(55.64, -24.82) * mm, "end": v(55.64, -28.18) * mm});
            skLineSegment(sketch, "E100", {"start": v(50.8, -7.93) * mm, "end": v(50.8, -12.87) * mm});
            skLineSegment(sketch, "E101", {"start": v(51.1, -24.52) * mm, "end": v(51.1, -28.18) * mm});
            skLineSegment(sketch, "E102", {"start": v(50.4, -14.25) * mm, "end": v(50.4, -22.75) * mm});
            skLineSegment(sketch, "E103", {"start": v(80.53, -11.78) * mm, "end": v(80.53, -23.54) * mm});
            skLineSegment(sketch, "E104", {"start": v(87.35, -12.47) * mm, "end": v(87.35, -22.55) * mm});
            skLineSegment(sketch, "E105", {"start": v(86.17, -7.33) * mm, "end": v(86.17, -11.19) * mm});
            skLineSegment(sketch, "E106", {"start": v(85.97, -24.03) * mm, "end": v(85.97, -28.18) * mm});
            skLineSegment(sketch, "E107", {"start": v(81.32, -6.15) * mm, "end": v(81.32, -10.3) * mm});
            skLineSegment(sketch, "E108", {"start": v(81.72, -24.43) * mm, "end": v(81.72, -28.18) * mm});
            skLineSegment(sketch, "E109", {"start": v(102.57, -20) * mm, "end": v(102.57, -23.16) * mm});
            skLineSegment(sketch, "E110", {"start": v(108, -20.36) * mm, "end": v(108, -16.52) * mm});
            skLineSegment(sketch, "E111", {"start": v(103.85, -12.47) * mm, "end": v(94.35, -10.25) * mm});
            skArc(sketch, "E112", {"start": v(14.3, -86.05) * mm, "mid": v(18.77, -82.28) * mm, "end": v(20.43, -76.68) * mm});
            skArc(sketch, "E113", {"start": v(20.43, -86.52) * mm, "mid": v(23.58, -82.07) * mm, "end": v(24.4, -76.68) * mm});
            skLineSegment(sketch, "E114", {"start": v(20.43, -76.68) * mm, "end": v(24.4, -76.68) * mm});
            skArc(sketch, "E115", {"start": v(58.91, -116.39) * mm, "mid": v(70.18, -118.32) * mm, "end": v(81.26, -115.52) * mm});
            skArc(sketch, "E116", {"start": v(14.3, -86.05) * mm, "mid": v(34.94, -103.68) * mm, "end": v(58.91, -116.39) * mm});
            skLineSegment(sketch, "E117", {"start": v(113.23, -76.68) * mm, "end": v(116.82, -76.68) * mm});
            skArc(sketch, "E118", {"start": v(116.82, -76.68) * mm, "mid": v(118.6, -82.75) * mm, "end": v(123.55, -86.69) * mm});
            skArc(sketch, "E119", {"start": v(113.23, -76.68) * mm, "mid": v(113.82, -82.23) * mm, "end": v(117.5, -86.42) * mm});
            skArc(sketch, "E120", {"start": v(81.26, -115.52) * mm, "mid": v(103.44, -102.62) * mm, "end": v(123.55, -86.69) * mm});
            skArc(sketch, "E121", {"start": v(78.17, -112.75) * mm, "mid": v(98.57, -100.68) * mm, "end": v(117.5, -86.42) * mm});
            skArc(sketch, "E122", {"start": v(59.66, -112.75) * mm, "mid": v(68.91, -114.37) * mm, "end": v(78.17, -112.75) * mm});
            skArc(sketch, "E123", {"start": v(20.43, -86.52) * mm, "mid": v(38.66, -101.7) * mm, "end": v(59.66, -112.75) * mm});
            skArc(sketch, "E124", {"start": v(108, -16.52) * mm, "mid": v(106.5, -13.92) * mm, "end": v(103.85, -12.47) * mm});
            skArc(sketch, "E125", {"start": v(102.57, -20) * mm, "mid": v(104.2, -17.67) * mm, "end": v(102.32, -15.54) * mm});
            skArc(sketch, "E126", {"start": v(104.1, -24.8) * mm, "mid": v(103.65, -23.68) * mm, "end": v(102.57, -23.16) * mm});
            skArc(sketch, "E127", {"start": v(107.07, -21.39) * mm, "mid": v(107.73, -21.05) * mm, "end": v(108, -20.36) * mm});
            skArc(sketch, "E128", {"start": v(108.08, -24.81) * mm, "mid": v(107.82, -23.55) * mm, "end": v(107.07, -22.5) * mm});
            skLineSegment(sketch, "E129", {"start": v(107.07, -21.39) * mm, "end": v(107.07, -22.5) * mm});
            skArc(sketch, "E130", {"start": v(50.8, -7.93) * mm, "mid": v(48.14, -9.02) * mm, "end": v(47.04, -11.67) * mm});
            skArc(sketch, "E131", {"start": v(50.4, -22.75) * mm, "mid": v(50.58, -23.7) * mm, "end": v(51.1, -24.52) * mm});
            skArc(sketch, "E132", {"start": v(50.8, -12.87) * mm, "mid": v(50.5, -13.53) * mm, "end": v(50.4, -14.25) * mm});
            skArc(sketch, "E133", {"start": v(47.04, -25.65) * mm, "mid": v(48.37, -28.04) * mm, "end": v(51.1, -28.18) * mm});
            skArc(sketch, "E134", {"start": v(55.64, -24.82) * mm, "mid": v(56.5, -24.11) * mm, "end": v(56.82, -23.04) * mm});
            skArc(sketch, "E135", {"start": v(56.82, -11.78) * mm, "mid": v(56.47, -10.6) * mm, "end": v(55.54, -9.8) * mm});
            skArc(sketch, "E136", {"start": v(60.22, -8.49) * mm, "mid": v(58.63, -5.82) * mm, "end": v(55.54, -5.95) * mm});
            skArc(sketch, "E137", {"start": v(55.64, -28.18) * mm, "mid": v(58.72, -28.04) * mm, "end": v(60.22, -25.35) * mm});
            skArc(sketch, "E138", {"start": v(77.1, -25.13) * mm, "mid": v(78.6, -27.9) * mm, "end": v(81.72, -28.18) * mm});
            skArc(sketch, "E139", {"start": v(81.32, -6.15) * mm, "mid": v(78.56, -5.9) * mm, "end": v(77.1, -8.25) * mm});
            skArc(sketch, "E140", {"start": v(80.53, -23.54) * mm, "mid": v(80.9, -24.28) * mm, "end": v(81.72, -24.43) * mm});
            skArc(sketch, "E141", {"start": v(81.32, -10.3) * mm, "mid": v(80.74, -10.94) * mm, "end": v(80.53, -11.78) * mm});
            skArc(sketch, "E142", {"start": v(87.35, -12.47) * mm, "mid": v(87.01, -11.6) * mm, "end": v(86.17, -11.19) * mm});
            skArc(sketch, "E143", {"start": v(90.57, -10.83) * mm, "mid": v(89, -8.3) * mm, "end": v(86.17, -7.33) * mm});
            skArc(sketch, "E144", {"start": v(85.97, -28.18) * mm, "mid": v(89.19, -27.18) * mm, "end": v(90.57, -24.11) * mm});
            skArc(sketch, "E145", {"start": v(85.97, -24.03) * mm, "mid": v(86.95, -23.56) * mm, "end": v(87.35, -22.55) * mm});
            skArc(sketch, "E146", {"start": v(121.07, -167.51) * mm, "mid": v(129.07, -141.67) * mm, "end": v(134.34, -115.13) * mm});
            skArc(sketch, "E147", {"start": v(121.07, -167.51) * mm, "mid": v(127, -140.97) * mm, "end": v(132.16, -114.26) * mm});
            skLineSegment(sketch, "E148", {"start": v(134.34, -115.13) * mm, "end": v(132.16, -114.26) * mm});
            skArc(sketch, "E149", {"start": v(126.34, -29.94) * mm, "mid": v(131.24, -26.23) * mm, "end": v(135.18, -21.5) * mm});
            skArc(sketch, "E150", {"start": v(133.44, -20.78) * mm, "mid": v(129.66, -25.18) * mm, "end": v(126.34, -29.94) * mm});
            skArc(sketch, "E151", {"start": v(135.18, -21.5) * mm, "mid": v(134.58, -20.5) * mm, "end": v(133.44, -20.78) * mm});
            skFitSpline(sketch, "E152", {"points": [v(143.8, -27.23) * mm, v(141.88, -23.6) * mm, v(139.94, -23.97) * mm, v(140.22, -27.36) * mm, v(142.95, -30.9) * mm, v(143.5, -29.6) * mm, v(142.2, -27.58) * mm, v(140.85, -25.43) * mm, v(142.77, -26.4) * mm, v(143.8, -27.23) * mm]});
            skFitSpline(sketch, "E153", {"points": [v(137.08, -22.64) * mm, v(134.38, -29.08) * mm, v(134.47, -30.48) * mm, v(136.62, -27.54) * mm, v(138.3, -22.64) * mm, v(137.08, -22.64) * mm]});
            skLineSegment(sketch, "E154", {"start": v(28.96, -79.76) * mm, "end": v(28.96, -85) * mm});
            skLineSegment(sketch, "E155", {"start": v(33.58, -81.98) * mm, "end": v(33.58, -84.94) * mm});
            skLineSegment(sketch, "E156", {"start": v(43.73, -98.6) * mm, "end": v(43.73, -94.1) * mm});
            skLineSegment(sketch, "E157", {"start": v(43.73, -94.1) * mm, "end": v(34.65, -87.1) * mm});
            skLineSegment(sketch, "E158", {"start": v(43.73, -98.6) * mm, "end": v(30.73, -88.6) * mm});
            skLineSegment(sketch, "E159", {"start": v(32.04, -76.68) * mm, "end": v(40.56, -76.68) * mm});
            skLineSegment(sketch, "E160", {"start": v(40.56, -76.68) * mm, "end": v(40.56, -80.57) * mm});
            skLineSegment(sketch, "E161", {"start": v(40.56, -80.57) * mm, "end": v(35, -80.57) * mm});
            skLineSegment(sketch, "E162", {"start": v(101.87, -89.34) * mm, "end": v(92.66, -94.66) * mm});
            skLineSegment(sketch, "E163", {"start": v(92.66, -94.66) * mm, "end": v(92.66, -99.08) * mm});
            skLineSegment(sketch, "E164", {"start": v(92.66, -99.08) * mm, "end": v(105.35, -91) * mm});
            skLineSegment(sketch, "E165", {"start": v(106.81, -89.06) * mm, "end": v(106.81, -85.8) * mm});
            skLineSegment(sketch, "E166", {"start": v(105, -83.7) * mm, "end": v(98.03, -83.7) * mm});
            skLineSegment(sketch, "E167", {"start": v(98.03, -80.7) * mm, "end": v(106.5, -80.7) * mm});
            skLineSegment(sketch, "E168", {"start": v(106.5, -80.7) * mm, "end": v(106.5, -76.36) * mm});
            skLineSegment(sketch, "E169", {"start": v(106.5, -76.36) * mm, "end": v(96.86, -76.36) * mm});
            skArc(sketch, "E170", {"start": v(96.86, -76.36) * mm, "mid": v(93.85, -77.7) * mm, "end": v(92.62, -80.74) * mm});
            skArc(sketch, "E171", {"start": v(101.87, -89.34) * mm, "mid": v(102.43, -88.36) * mm, "end": v(101.87, -87.37) * mm});
            skArc(sketch, "E172", {"start": v(81.27, -101.19) * mm, "mid": v(82.19, -102.81) * mm, "end": v(84.05, -102.87) * mm});
            skArc(sketch, "E173", {"start": v(61.64, -76.68) * mm, "mid": v(58.95, -77.77) * mm, "end": v(57.6, -80.34) * mm});
            skArc(sketch, "E174", {"start": v(28.96, -85) * mm, "mid": v(29.43, -87.01) * mm, "end": v(30.73, -88.6) * mm});
            skArc(sketch, "E175", {"start": v(32.04, -76.68) * mm, "mid": v(29.86, -77.58) * mm, "end": v(28.96, -79.76) * mm});
            skArc(sketch, "E176", {"start": v(35, -80.57) * mm, "mid": v(34, -80.99) * mm, "end": v(33.58, -81.98) * mm});
            skArc(sketch, "E177", {"start": v(83.18, -76.11) * mm, "mid": v(81.8, -76.67) * mm, "end": v(81.24, -78.04) * mm});
            skArc(sketch, "E178", {"start": v(63.93, -81.2) * mm, "mid": v(62.95, -81.6) * mm, "end": v(62.54, -82.57) * mm});
            skArc(sketch, "E179", {"start": v(57.34, -102.7) * mm, "mid": v(57.76, -104.78) * mm, "end": v(59.42, -106.1) * mm});
            skArc(sketch, "E180", {"start": v(62.34, -100.82) * mm, "mid": v(62.75, -102.24) * mm, "end": v(63.9, -103.17) * mm});
            skLineSegment(sketch, "E181", {"start": v(43.27, -77.22) * mm, "end": v(47.62, -87.25) * mm});
            skLineSegment(sketch, "E182", {"start": v(47.62, -87.25) * mm, "end": v(47.62, -100.93) * mm});
            skLineSegment(sketch, "E183", {"start": v(47.62, -100.93) * mm, "end": v(51.05, -102.61) * mm});
            skLineSegment(sketch, "E184", {"start": v(51.05, -102.61) * mm, "end": v(51.05, -88.25) * mm});
            skLineSegment(sketch, "E185", {"start": v(51.05, -88.25) * mm, "end": v(56.46, -77.05) * mm});
            skLineSegment(sketch, "E186", {"start": v(56.46, -77.05) * mm, "end": v(53.18, -77.05) * mm});
            skLineSegment(sketch, "E187", {"start": v(53.18, -77.05) * mm, "end": v(50.06, -83.52) * mm});
            skLineSegment(sketch, "E188", {"start": v(50.06, -83.52) * mm, "end": v(47.33, -77.22) * mm});
            skLineSegment(sketch, "E189", {"start": v(47.33, -77.22) * mm, "end": v(43.27, -77.22) * mm});
            skLineSegment(sketch, "E190", {"start": v(67.53, -109.95) * mm, "end": v(59.42, -106.1) * mm});
            skLineSegment(sketch, "E191", {"start": v(57.34, -102.7) * mm, "end": v(57.6, -80.34) * mm});
            skLineSegment(sketch, "E192", {"start": v(61.64, -76.68) * mm, "end": v(67.3, -76.68) * mm});
            skLineSegment(sketch, "E193", {"start": v(67.3, -76.68) * mm, "end": v(67.3, -81.2) * mm});
            skLineSegment(sketch, "E194", {"start": v(67.3, -81.2) * mm, "end": v(63.93, -81.2) * mm});
            skLineSegment(sketch, "E195", {"start": v(62.54, -82.57) * mm, "end": v(62.34, -100.82) * mm});
            skLineSegment(sketch, "E196", {"start": v(63.9, -103.17) * mm, "end": v(67.56, -104.67) * mm});
            skLineSegment(sketch, "E197", {"start": v(67.56, -104.67) * mm, "end": v(67.53, -109.95) * mm});
            skLineSegment(sketch, "E198", {"start": v(75.94, -76.7) * mm, "end": v(70.83, -76.7) * mm});
            skLineSegment(sketch, "E199", {"start": v(70.83, -76.7) * mm, "end": v(70.83, -106.94) * mm});
            skLineSegment(sketch, "E200", {"start": v(73.12, -108.37) * mm, "end": v(79.34, -105.34) * mm});
            skLineSegment(sketch, "E201", {"start": v(79.34, -105.34) * mm, "end": v(79.34, -100.83) * mm});
            skLineSegment(sketch, "E202", {"start": v(79.34, -100.83) * mm, "end": v(75.94, -102.49) * mm});
            skLineSegment(sketch, "E203", {"start": v(75.94, -102.49) * mm, "end": v(75.94, -76.7) * mm});
            skLineSegment(sketch, "E204", {"start": v(84.05, -102.87) * mm, "end": v(90.16, -99.67) * mm});
            skLineSegment(sketch, "E205", {"start": v(90.16, -99.67) * mm, "end": v(90.16, -96.1) * mm});
            skLineSegment(sketch, "E206", {"start": v(90.16, -96.1) * mm, "end": v(85.71, -98.43) * mm});
            skLineSegment(sketch, "E207", {"start": v(85.71, -98.43) * mm, "end": v(85.77, -90.92) * mm});
            skLineSegment(sketch, "E208", {"start": v(85.77, -90.92) * mm, "end": v(89.95, -90.79) * mm});
            skLineSegment(sketch, "E209", {"start": v(89.95, -90.79) * mm, "end": v(89.95, -86.5) * mm});
            skLineSegment(sketch, "E210", {"start": v(89.95, -86.5) * mm, "end": v(85.51, -86.64) * mm});
            skLineSegment(sketch, "E211", {"start": v(85.51, -86.64) * mm, "end": v(85.51, -80.3) * mm});
            skLineSegment(sketch, "E212", {"start": v(85.51, -80.3) * mm, "end": v(90.3, -80.3) * mm});
            skLineSegment(sketch, "E213", {"start": v(90.3, -80.3) * mm, "end": v(90.3, -76.16) * mm});
            skLineSegment(sketch, "E214", {"start": v(90.3, -76.16) * mm, "end": v(83.18, -76.11) * mm});
            skLineSegment(sketch, "E215", {"start": v(81.24, -78.04) * mm, "end": v(81.27, -101.19) * mm});
            skLineSegment(sketch, "E216", {"start": v(101.87, -87.37) * mm, "end": v(95.2, -87.37) * mm});
            skArc(sketch, "E217", {"start": v(92.62, -84.8) * mm, "mid": v(93.38, -86.62) * mm, "end": v(95.2, -87.37) * mm});
            skLineSegment(sketch, "E218", {"start": v(92.62, -80.74) * mm, "end": v(92.62, -84.8) * mm});
            skArc(sketch, "E219", {"start": v(33.58, -84.94) * mm, "mid": v(33.86, -86.15) * mm, "end": v(34.65, -87.1) * mm});
            skPoint(sketch, "E220.visualSharp", {"position": v(70.83, -109.48) * mm});
            skArc(sketch, "E220.filletArc", {"start": v(70.83, -106.94) * mm, "mid": v(71.58, -108.3) * mm, "end": v(73.12, -108.37) * mm});
            skArc(sketch, "E221", {"start": v(98.03, -80.7) * mm, "mid": v(96.53, -82.2) * mm, "end": v(98.03, -83.7) * mm});
            skArc(sketch, "E222", {"start": v(106.81, -85.8) * mm, "mid": v(106.3, -84.41) * mm, "end": v(105, -83.7) * mm});
            skArc(sketch, "E223", {"start": v(105.35, -91) * mm, "mid": v(106.29, -90.18) * mm, "end": v(106.81, -89.06) * mm});
            skSolve(sketch);
        }
        {
            var Q0;
            Q0 = qSketchRegion(id + "F0", true);
            extrude(context, id + "F1", {"entities" : qUnion([Q0]), "depth" : 3.17 * mm});
        }
    });
